# Revit family: Food-Service-Equipment_Oscartek_Rdpc1700_Standard_cat
name_source: partatom
category: Specialty Equipment
units: mm (PartAtom-declared; Revit-internal decimal feet)

## family parameters
Always vertical = Yes
Classification Number = 23.40.40.11.17
Cut with Voids When Loaded = No
Enable Cutting in Views = No
Maintain Annotation Orientation = No
Part Type = Normal
Room Calculation Point = No
Round Connector Dimension = Use Diameter
Shared = No
Work Plane-Based = No

## types (1)
- Food-Service-Equipment_Oscartek_Rdpc1700_Standard_cat
    Apparent Power = 1035 VA
    Building Codes = https://www.arcat.com
    CSI Master Format = Refrigerated Food Storage Cases
    CSI MasterFormat = 11 41 13
    Conn Conduit = Yes
    Construction Details = http://www.oscartek.com
    Cycle = 50 Hz
    Default Elevation = 0"
    Description = ROSA DELI/PASTRY/CHOCOLATE SHOWCASE
    FL Amps = 5 A
    Green Building-LEED = https://www.arcat.com
    Indirect Waste Connection Height = 0"
    Installation-Fabrication = http://www.oscartek.com
    Manufacturer = OSCARTEK
    Manufacturer Fax = 650-342-7400
    Manufacturer Website = http://www.oscartek.com
    Max Overcurrent Protection = 0 A
    Min Ckt Ampacity = 0 A
    Model = RDPC1700
    Phase = 1
    Product Data = http://www.oscartek.com
    Revision = R1_2018-10
    Sales Information = http://www.oscartek.com
    Specification = https://www.arcat.com
    Test Data = http://www.oscartek.com
    Type Comments = As Specified
    URL = www.oscartek.com
    URL Cutsheet = www.oscartek.com
    Volts = 230 V
    Watts = 885 W
    Weight in Pounds = 346
    Width = 67"

## geometry (parser evidence)
native form markers: Blend x31, Sweep x4
no freeform markers — native parametric forms only
